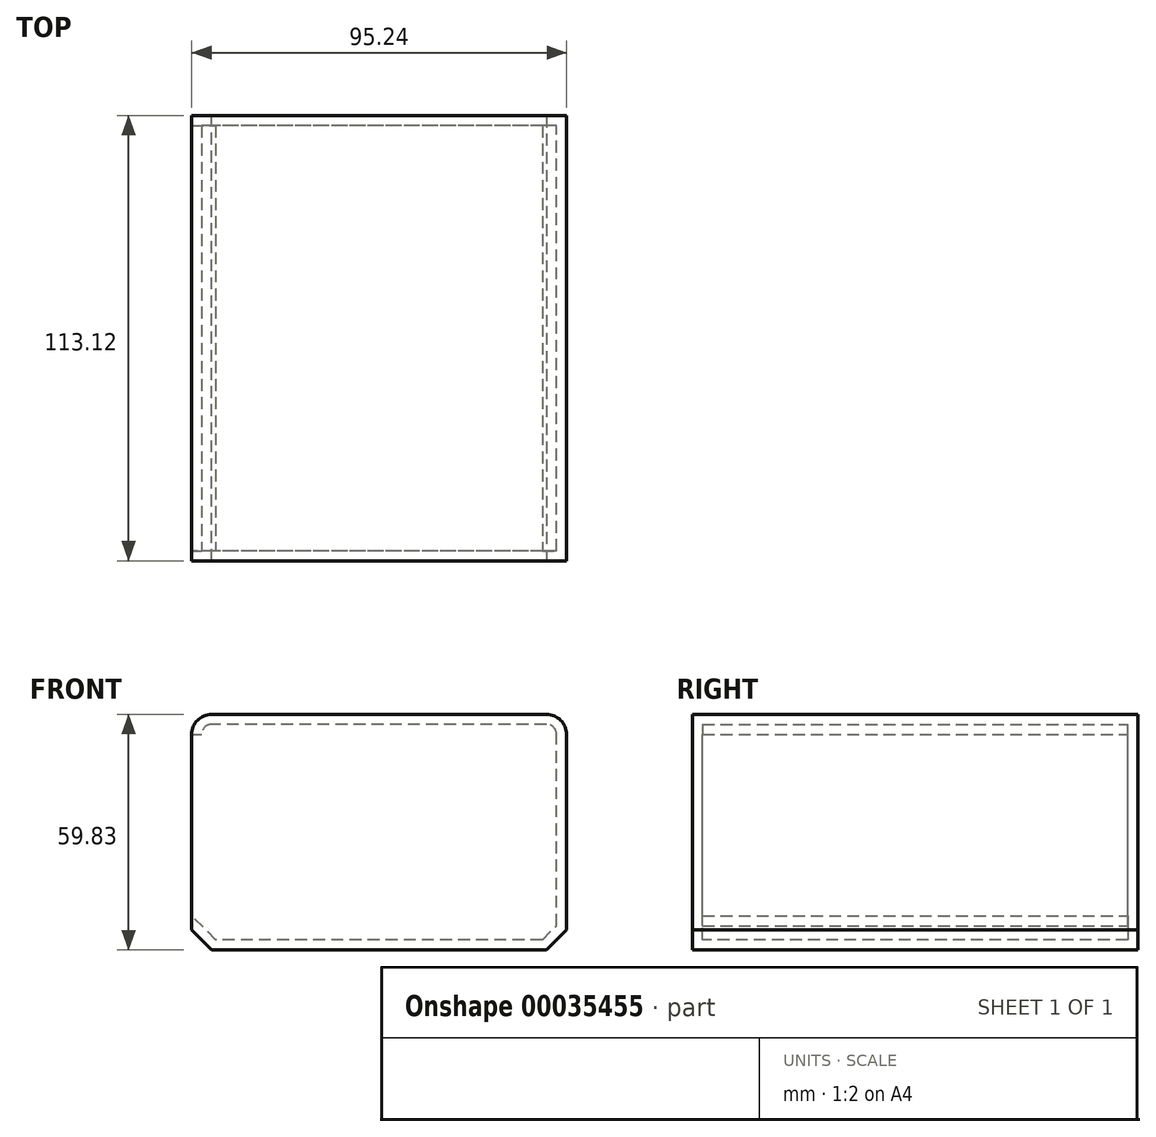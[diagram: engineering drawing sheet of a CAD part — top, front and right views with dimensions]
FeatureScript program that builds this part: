
annotation { "Feature Type Name" : "Feature", "Feature Type Description" : "" }
export const myFeature = defineFeature(function(context is Context, id is Id, definition is map)
    precondition{}
    {
        {
            var Q0;
            Q0=qCreatedBy(makeId("Front.planeOp"),FACE);
            var sketch = newSketch(context, id + "F0", { "sketchPlane" : qUnion([Q0])});
            skLineSegment(sketch, "E0.rect.bottom", {"start": v(0, 8.75) * mm, "end": v(-95.24, 8.75) * mm});
            skLineSegment(sketch, "E0.rect.top", {"start": v(0, 68.58) * mm, "end": v(-95.24, 68.58) * mm});
            skLineSegment(sketch, "E0.rect.left", {"start": v(0, 8.75) * mm, "end": v(0, 68.58) * mm});
            skLineSegment(sketch, "E0.rect.right", {"start": v(-95.24, 8.75) * mm, "end": v(-95.24, 68.58) * mm});
            skPoint(sketch, "E0.rect.middle", {"position": v(-47.62, 38.66) * mm});
            skSolve(sketch);
        }
        {
            var Q0;
            Q0=makeQuery(id+"F0.imprint","IMPRINT",FACE,{"disambiguationData":[TD([[makeQuery(id+"F0.imprint","IMPRINT",EDGE,{"derivedFrom":sQuery(id+"F0.wireOp",EDGE,"E0.rect.bottom")}),-1.0]])]});
            extrude(context, id + "F1", {"entities" : qUnion([Q0]), "depth" : 113.12 * mm});
        }
        {
            var Q0;
            Q0=makeQuery(id+"F1.opExtrude","SWEPT_EDGE",EDGE,{"disambiguationData":[OSD([sQuery(id+"F0.wireOp",EDGE,"E0.rect.top"),sQuery(id+"F0.wireOp",EDGE,"E0.rect.right")])]});
            var Q1;
            Q1=makeQuery(id+"F1.opExtrude","SWEPT_EDGE",EDGE,{"disambiguationData":[OSD([sQuery(id+"F0.wireOp",EDGE,"E0.rect.top"),sQuery(id+"F0.wireOp",EDGE,"E0.rect.left")])]});
            fillet(context, id + "F2", {"entities" : qUnion([Q0, Q1]), "radius" : 5.08 * mm, "tangentPropagation" : true, "allowEdgeOverflow" : false});
        }
        {
            var Q0;
            Q0=makeQuery(id+"F1.opExtrude","SWEPT_EDGE",EDGE,{"disambiguationData":[OSD([sQuery(id+"F0.wireOp",EDGE,"E0.rect.bottom"),sQuery(id+"F0.wireOp",EDGE,"E0.rect.right")])]});
            var Q1;
            Q1=makeQuery(id+"F1.opExtrude","SWEPT_EDGE",EDGE,{"disambiguationData":[OSD([sQuery(id+"F0.wireOp",EDGE,"E0.rect.bottom"),sQuery(id+"F0.wireOp",EDGE,"E0.rect.left")])]});
            chamfer(context, id + "F3", {"entities" : qUnion([Q0, Q1]), "width" : 5.08 * mm, "tangentPropagation" : true});
        }
        {
            var Q0;
            Q0=makeQuery(id+"F1.opExtrude","SWEPT_FACE",FACE,{"disambiguationData":[OSD([sQuery(id+"F0.wireOp",EDGE,"E0.rect.right")])]});
            shell(context, id + "F4", {"entities" : qUnion([Q0]), "thickness" : 2.54 * mm});
        }
    });
